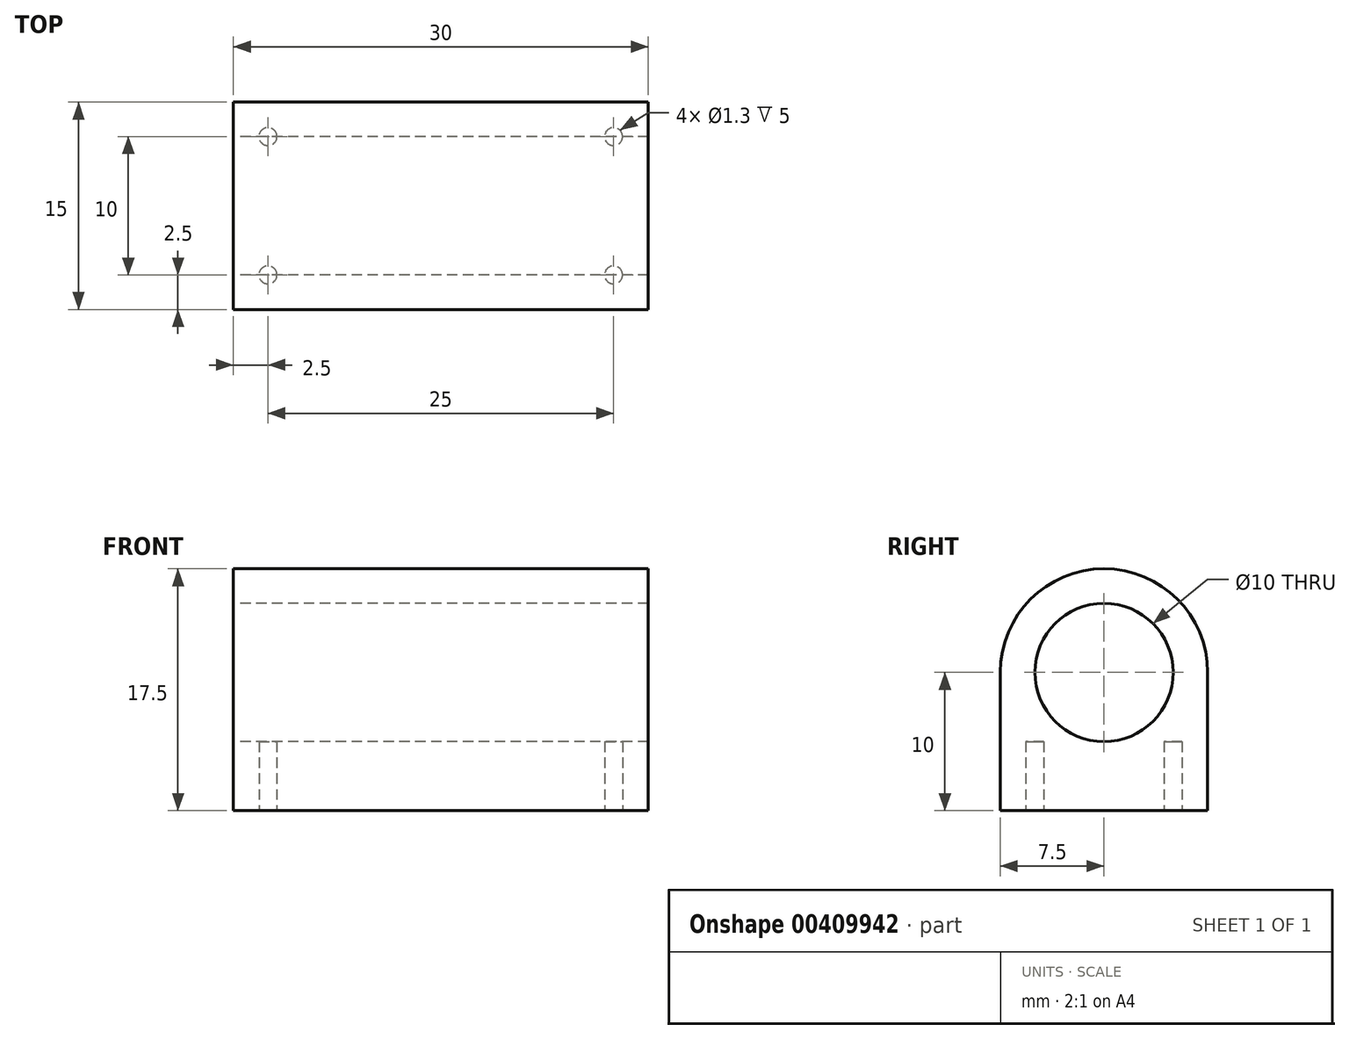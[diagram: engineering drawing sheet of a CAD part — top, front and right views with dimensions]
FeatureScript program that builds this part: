
annotation { "Feature Type Name" : "Feature", "Feature Type Description" : "" }
export const myFeature = defineFeature(function(context is Context, id is Id, definition is map)
    precondition{}
    {
        {
            var Q0;
            Q0=qCreatedBy(makeId("Right.planeOp"),FACE);
            var sketch = newSketch(context, id + "F0", { "sketchPlane" : qUnion([Q0])});
            skCircle(sketch, "E0", {"center": v(0, 0) * mm, "radius": 5 * mm});
            skArc(sketch, "E1", {"start": v(7.5, 0) * mm, "mid": v(0, 7.5) * mm, "end": v(-7.5, 0) * mm});
            skLineSegment(sketch, "E2.bottom", {"start": v(-7.5, 0) * mm, "end": v(7.5, 0) * mm});
            skLineSegment(sketch, "E2.top", {"start": v(-7.5, -10) * mm, "end": v(7.5, -10) * mm});
            skLineSegment(sketch, "E2.left", {"start": v(-7.5, 0) * mm, "end": v(-7.5, -10) * mm});
            skLineSegment(sketch, "E2.right", {"start": v(7.5, 0) * mm, "end": v(7.5, -10) * mm});
            skSolve(sketch);
        }
        {
            var Q0;
            {var subQ4=sQuery(id+"F0.wireOp",EDGE,"E1");Q0=makeQuery(id+"F0.imprint","IMPRINT",FACE,{"disambiguationData":[TD([[makeQuery(id+"F0.imprint","IMPRINT",EDGE,{"derivedFrom":subQ4}),1.0]])]});}
            var Q1;
            Q1=makeQuery(id+"F0.imprint","IMPRINT",FACE,{"disambiguationData":[TD([[makeQuery(id+"F0.imprint","IMPRINT",EDGE,{"derivedFrom":sQuery(id+"F0.wireOp",EDGE,"E2.top")}),1.0]])]});
            extrude(context, id + "F1", {"entities" : qUnion([Q0, Q1]), "depth" : 30 * mm});
        }
        {
            var Q0;
            Q0=makeQuery(id+"F1.opExtrude","SWEPT_FACE",FACE,{"disambiguationData":[OSD([sQuery(id+"F0.wireOp",EDGE,"E2.top")])]});
            var sketch = newSketch(context, id + "F2", { "sketchPlane" : qUnion([Q0])});
            skCircle(sketch, "E3", {"center": v(2.5, -5) * mm, "radius": 0.65 * mm});
            skCircle(sketch, "E4", {"center": v(2.5, 5) * mm, "radius": 0.65 * mm});
            skCircle(sketch, "E5", {"center": v(27.5, -5) * mm, "radius": 0.65 * mm});
            skCircle(sketch, "E6", {"center": v(27.5, 5) * mm, "radius": 0.65 * mm});
            skSolve(sketch);
        }
        {
            var Q0;
            Q0=makeQuery(id+"F2.imprint","IMPRINT",FACE,{"disambiguationData":[TD([[makeQuery(id+"F2.imprint","IMPRINT",EDGE,{"derivedFrom":sQuery(id+"F2.wireOp",EDGE,"E6")}),1.0]])]});
            var Q1;
            Q1=makeQuery(id+"F2.imprint","IMPRINT",FACE,{"disambiguationData":[TD([[makeQuery(id+"F2.imprint","IMPRINT",EDGE,{"derivedFrom":sQuery(id+"F2.wireOp",EDGE,"E5")}),1.0]])]});
            var Q2;
            Q2=makeQuery(id+"F2.imprint","IMPRINT",FACE,{"disambiguationData":[TD([[makeQuery(id+"F2.imprint","IMPRINT",EDGE,{"derivedFrom":sQuery(id+"F2.wireOp",EDGE,"E4")}),1.0]])]});
            var Q3;
            Q3=makeQuery(id+"F2.imprint","IMPRINT",FACE,{"disambiguationData":[TD([[makeQuery(id+"F2.imprint","IMPRINT",EDGE,{"derivedFrom":sQuery(id+"F2.wireOp",EDGE,"E3")}),1.0]])]});
            extrude(context, id + "F3", {"entities" : qUnion([Q0, Q1, Q2, Q3]), "operationType" : NewBodyOperationType.REMOVE, "oppositeDirection" : true, "depth" : 5 * mm});
        }
    });
